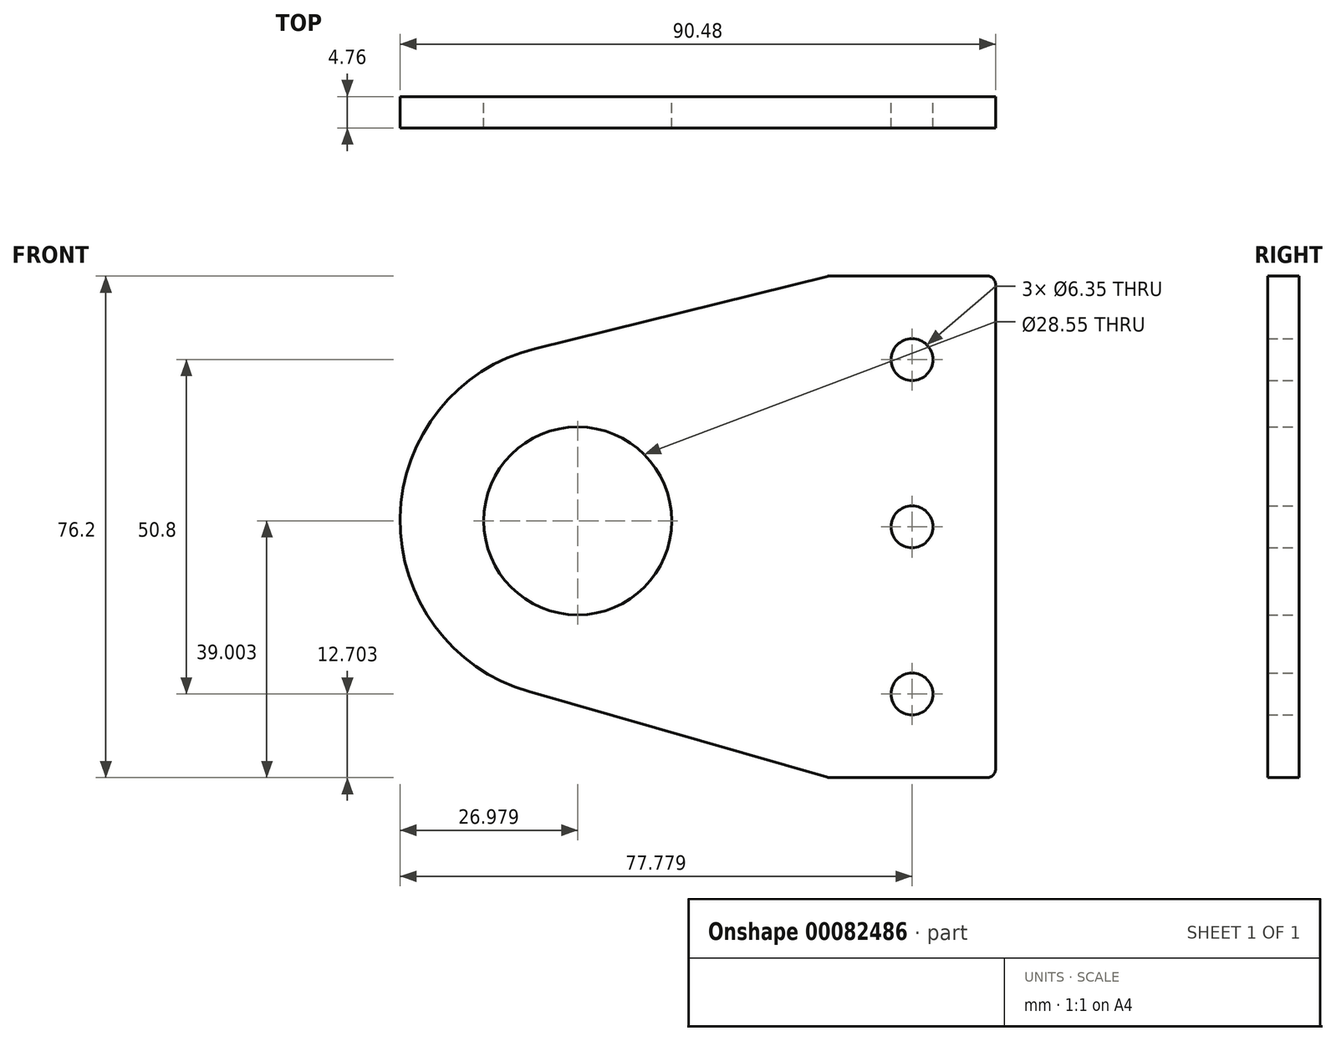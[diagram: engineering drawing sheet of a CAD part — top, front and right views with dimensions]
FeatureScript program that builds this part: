
annotation { "Feature Type Name" : "Feature", "Feature Type Description" : "" }
export const myFeature = defineFeature(function(context is Context, id is Id, definition is map)
    precondition{}
    {
        {
            var Q0;
            Q0=qCreatedBy(makeId("Front.planeOp"),FACE);
            var sketch = newSketch(context, id + "F0", { "sketchPlane" : qUnion([Q0])});
            skLineSegment(sketch, "E0", {"start": v(-29.3, 61.5) * mm, "end": v(-29.3, -14.7) * mm});
            skPoint(sketch, "E1", {"position": v(-42, 48.8) * mm});
            skPoint(sketch, "E2", {"position": v(-42, -2) * mm});
            skPoint(sketch, "E3", {"position": v(-42, 23.4) * mm});
            skCircle(sketch, "E4", {"center": v(-92.8, 24.3) * mm, "radius": 14.27 * mm});
            skLineSegment(sketch, "E5", {"start": v(-29.3, -14.7) * mm, "end": v(-54.7, -14.7) * mm});
            skArc(sketch, "E6", {"start": v(-99.26, 50.49) * mm, "mid": v(-119.76, 24.8) * mm, "end": v(-100.23, -1.63) * mm});
            skLineSegment(sketch, "E7", {"start": v(-54.7, -14.7) * mm, "end": v(-100.23, -1.63) * mm});
            skLineSegment(sketch, "E8", {"start": v(-29.3, 61.5) * mm, "end": v(-54.7, 61.5) * mm});
            skLineSegment(sketch, "E9", {"start": v(-54.7, 61.5) * mm, "end": v(-99.26, 50.49) * mm});
            skSolve(sketch);
        }
        {
            var Q0;
            Q0=makeQuery(id+"F0.imprint","IMPRINT",FACE,{"disambiguationData":[TD([[makeQuery(id+"F0.imprint","IMPRINT",EDGE,{"derivedFrom":sQuery(id+"F0.wireOp",EDGE,"E0")}),-1.0]])]});
            extrude(context, id + "F1", {"entities" : qUnion([Q0]), "depth" : 4.76 * mm});
        }
        {
            var Q0;
            Q0=sQuery(id+"F0.wireOp",VERTEX,"E1");
            var Q1;
            Q1=sQuery(id+"F0.wireOp",VERTEX,"E3");
            var Q2;
            Q2=sQuery(id+"F0.wireOp",VERTEX,"E2");
            var Q3;
            Q3=makeQuery(id+"F1.opExtrude","SWEPT_BODY",BODY,{"disambiguationData":[OSD([sQuery(id+"F0.wireOp",EDGE,"E0"),sQuery(id+"F0.wireOp",EDGE,"E4"),sQuery(id+"F0.wireOp",EDGE,"E5"),sQuery(id+"F0.wireOp",EDGE,"E6"),sQuery(id+"F0.wireOp",EDGE,"E7"),sQuery(id+"F0.wireOp",EDGE,"E8"),sQuery(id+"F0.wireOp",EDGE,"E9")])]});
            hole(context, id + "F2", {"style" : HoleStyle.SIMPLE, "endStyle" : HoleEndStyle.THROUGH, "oppositeDirection" : true, "holeDiameter" : 6.35 * mm, "locations" : qUnion([Q0, Q1, Q2]), "scope" : qUnion([Q3]), "isTappedThrough" : true});
        }
        {
            var Q0;
            Q0=makeQuery(id+"F1.opExtrude","SWEPT_EDGE",EDGE,{"disambiguationData":[OSD([sQuery(id+"F0.wireOp",EDGE,"E0"),sQuery(id+"F0.wireOp",EDGE,"E8")])]});
            var Q1;
            Q1=makeQuery(id+"F1.opExtrude","SWEPT_EDGE",EDGE,{"disambiguationData":[OSD([sQuery(id+"F0.wireOp",EDGE,"E0"),sQuery(id+"F0.wireOp",EDGE,"E5")])]});
            var Q2;
            Q2=makeQuery(id+"F1.opExtrude","SWEPT_EDGE",EDGE,{"disambiguationData":[OSD([sQuery(id+"F0.wireOp",EDGE,"E8"),sQuery(id+"F0.wireOp",EDGE,"E9")])]});
            var Q3;
            Q3=makeQuery(id+"F1.opExtrude","SWEPT_EDGE",EDGE,{"disambiguationData":[OSD([sQuery(id+"F0.wireOp",EDGE,"E5"),sQuery(id+"F0.wireOp",EDGE,"E7")])]});
            fillet(context, id + "F3", {"entities" : qUnion([Q0, Q1, Q2, Q3]), "radius" : 1.27 * mm, "tangentPropagation" : true, "allowEdgeOverflow" : false});
        }
    });
